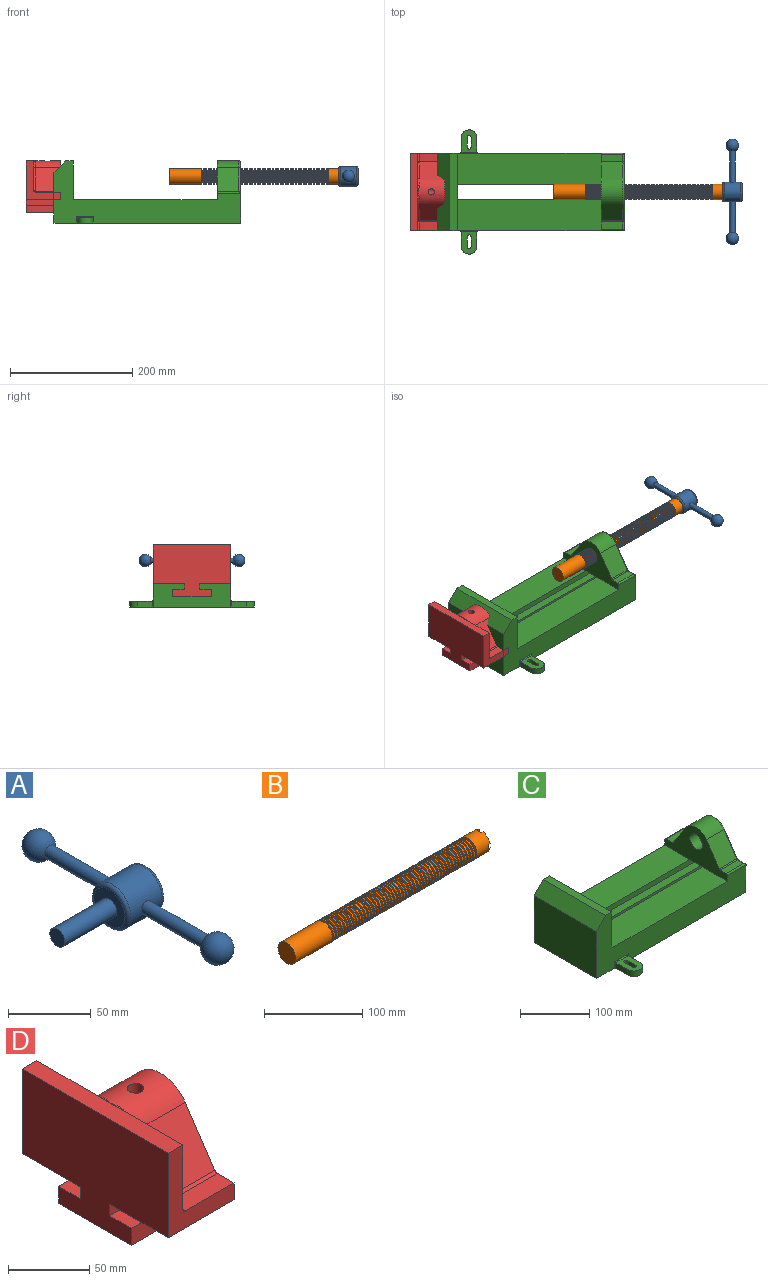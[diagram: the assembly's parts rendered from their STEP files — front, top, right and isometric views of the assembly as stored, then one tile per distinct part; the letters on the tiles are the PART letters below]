
ASSEMBLY  parts=4 mates=4
PART A: 11 faces, bbox 76.2x172.7x34.4 mm
  f0: sphere r=10.16mm, area 1231.8mm2, adj f1
  f1: cylinder r=4.45mm len=51.82mm, axis (0,1,0), area 1438.5mm2, adj f0,f4
  f2: sphere r=10.16mm, area 1231.8mm2, adj f3
  f3: cylinder r=4.45mm len=51.82mm, axis (0,1,0), area 1438.5mm2, adj f2,f4
  f4: cylinder r=15.88mm len=31.75mm, axis (-1,0,0), area 2534.7mm2, adj f1,f3,f9,f10
  f5: cylinder r=6.35mm len=44.45mm, axis (-1,0,0), area 1773.5mm2, adj f6,f8
  f6: plane 12.7x12.7mm, normal (-1,0,0), area 126.7mm2, adj f5
  f7: plane 26.67x26.67mm, normal (1,0,0), area 558.6mm2, adj f10
  f8: plane 26.67x26.67mm, normal (-1,0,0), area 432mm2, adj f5,f9
  f9: torus R=13.33mm, axis (1,0,0), area 374.8mm2, adj f4,f8
  f10: torus R=13.33mm, axis (1,0,0), area 374.8mm2, adj f4,f7
PART B: 220 faces, bbox 279.4x25.4x25.4 mm
  f0: cylinder r=12.7mm len=25.4mm, axis (-1,0,0), area 1468.2mm2, adj f1,f2,f3,f5,f7,f208,f209,f210
  f1: plane 9.9x9.9mm, normal (1,0,0), area 62.3mm2, adj f0,f4,f213,f216
  f2: plane 9.9x9.9mm, normal (1,0,0), area 62.3mm2, adj f0,f4,f210,f218
  f3: plane 9.9x9.9mm, normal (1,0,0), area 62.3mm2, adj f0,f4,f209,f212
  f4: cylinder r=6.35mm len=25.4mm, axis (1,0,0), area 960.3mm2, adj f1,f2,f3,f5,f6,f208,f209,f210
  f5: plane 9.9x9.9mm, normal (1,0,0), area 62.3mm2, adj f0,f4,f215,f217
  f6: plane 12.7x12.7mm, normal (1,0,0), area 126.7mm2, adj f4
  f7: cone r=12.7mm half-angle=76deg, axis (1,0,0), area 188mm2, adj f0,f9
  f8: cone r=10.16mm half-angle=76deg, axis (-1,0,0), area 188mm2, adj f9,f10
  f9: cylinder r=10.16mm len=20.32mm, axis (1,0,0), area 81.1mm2, adj f7,f8
  f10: cylinder r=12.7mm len=25.4mm, axis (-1,0,0), area 131.7mm2, adj f8,f11
  f11: cone r=12.7mm half-angle=76deg, axis (1,0,0), area 188mm2, adj f10,f13
  f12: cone r=10.16mm half-angle=76deg, axis (-1,0,0), area 188mm2, adj f13,f14
  f13: cylinder r=10.16mm len=20.32mm, axis (1,0,0), area 81.1mm2, adj f11,f12
  f14: cylinder r=12.7mm len=25.4mm, axis (-1,0,0), area 131.7mm2, adj f12,f15
  f15: cone r=12.7mm half-angle=76deg, axis (1,0,0), area 188mm2, adj f14,f17
  f16: cone r=10.16mm half-angle=76deg, axis (-1,0,0), area 188mm2, adj f17,f18
  f17: cylinder r=10.16mm len=20.32mm, axis (1,0,0), area 81.1mm2, adj f15,f16
  f18: cylinder r=12.7mm len=25.4mm, axis (-1,0,0), area 131.7mm2, adj f16,f19
  f19: cone r=12.7mm half-angle=76deg, axis (1,0,0), area 188mm2, adj f18,f21
  f20: cone r=10.16mm half-angle=76deg, axis (-1,0,0), area 188mm2, adj f21,f22
  f21: cylinder r=10.16mm len=20.32mm, axis (1,0,0), area 81.1mm2, adj f19,f20
  f22: cylinder r=12.7mm len=25.4mm, axis (-1,0,0), area 131.7mm2, adj f20,f23
  f23: cone r=12.7mm half-angle=76deg, axis (1,0,0), area 188mm2, adj f22,f25
  f24: cone r=10.16mm half-angle=76deg, axis (-1,0,0), area 188mm2, adj f25,f26
  f25: cylinder r=10.16mm len=20.32mm, axis (1,0,0), area 81.1mm2, adj f23,f24
  f26: cylinder r=12.7mm len=25.4mm, axis (-1,0,0), area 131.7mm2, adj f24,f27
  f27: cone r=12.7mm half-angle=76deg, axis (1,0,0), area 188mm2, adj f26,f29
  f28: cone r=10.16mm half-angle=76deg, axis (-1,0,0), area 188mm2, adj f29,f30
  f29: cylinder r=10.16mm len=20.32mm, axis (1,0,0), area 81.1mm2, adj f27,f28
  f30: cylinder r=12.7mm len=25.4mm, axis (-1,0,0), area 131.7mm2, adj f28,f31
  f31: cone r=12.7mm half-angle=76deg, axis (1,0,0), area 188mm2, adj f30,f33
  f32: cone r=10.16mm half-angle=76deg, axis (-1,0,0), area 188mm2, adj f33,f34
  f33: cylinder r=10.16mm len=20.32mm, axis (1,0,0), area 81.1mm2, adj f31,f32
  f34: cylinder r=12.7mm len=25.4mm, axis (-1,0,0), area 131.7mm2, adj f32,f35
  f35: cone r=12.7mm half-angle=76deg, axis (1,0,0), area 188mm2, adj f34,f37
  f36: cone r=10.16mm half-angle=76deg, axis (-1,0,0), area 188mm2, adj f37,f38
  f37: cylinder r=10.16mm len=20.32mm, axis (1,0,0), area 81.1mm2, adj f35,f36
  f38: cylinder r=12.7mm len=25.4mm, axis (-1,0,0), area 131.7mm2, adj f36,f39
  f39: cone r=12.7mm half-angle=76deg, axis (1,0,0), area 188mm2, adj f38,f41
  f40: cone r=10.16mm half-angle=76deg, axis (-1,0,0), area 188mm2, adj f41,f42
  f41: cylinder r=10.16mm len=20.32mm, axis (1,0,0), area 81.1mm2, adj f39,f40
  f42: cylinder r=12.7mm len=25.4mm, axis (-1,0,0), area 131.7mm2, adj f40,f43
  f43: cone r=12.7mm half-angle=76deg, axis (1,0,0), area 188mm2, adj f42,f45
  f44: cone r=10.16mm half-angle=76deg, axis (-1,0,0), area 188mm2, adj f45,f46
  f45: cylinder r=10.16mm len=20.32mm, axis (1,0,0), area 81.1mm2, adj f43,f44
  f46: cylinder r=12.7mm len=25.4mm, axis (-1,0,0), area 131.7mm2, adj f44,f47
  f47: cone r=12.7mm half-angle=76deg, axis (1,0,0), area 188mm2, adj f46,f49
  f48: cone r=10.16mm half-angle=76deg, axis (-1,0,0), area 188mm2, adj f49,f50
  f49: cylinder r=10.16mm len=20.32mm, axis (1,0,0), area 81.1mm2, adj f47,f48
  f50: cylinder r=12.7mm len=25.4mm, axis (-1,0,0), area 131.7mm2, adj f48,f51
  f51: cone r=12.7mm half-angle=76deg, axis (1,0,0), area 188mm2, adj f50,f53
  f52: cone r=10.16mm half-angle=76deg, axis (-1,0,0), area 188mm2, adj f53,f54
  f53: cylinder r=10.16mm len=20.32mm, axis (1,0,0), area 81.1mm2, adj f51,f52
  f54: cylinder r=12.7mm len=25.4mm, axis (-1,0,0), area 131.7mm2, adj f52,f55
  f55: cone r=12.7mm half-angle=76deg, axis (1,0,0), area 188mm2, adj f54,f57
  f56: cone r=10.16mm half-angle=76deg, axis (-1,0,0), area 188mm2, adj f57,f58
  f57: cylinder r=10.16mm len=20.32mm, axis (1,0,0), area 81.1mm2, adj f55,f56
  f58: cylinder r=12.7mm len=25.4mm, axis (-1,0,0), area 131.7mm2, adj f56,f59
  f59: cone r=12.7mm half-angle=76deg, axis (1,0,0), area 188mm2, adj f58,f61
  f60: cone r=10.16mm half-angle=76deg, axis (-1,0,0), area 188mm2, adj f61,f62
  f61: cylinder r=10.16mm len=20.32mm, axis (1,0,0), area 81.1mm2, adj f59,f60
  f62: cylinder r=12.7mm len=25.4mm, axis (-1,0,0), area 131.7mm2, adj f60,f63
  f63: cone r=12.7mm half-angle=76deg, axis (1,0,0), area 188mm2, adj f62,f65
  f64: cone r=10.16mm half-angle=76deg, axis (-1,0,0), area 188mm2, adj f65,f66
  f65: cylinder r=10.16mm len=20.32mm, axis (1,0,0), area 81.1mm2, adj f63,f64
  f66: cylinder r=12.7mm len=25.4mm, axis (-1,0,0), area 131.7mm2, adj f64,f67
  f67: cone r=12.7mm half-angle=76deg, axis (1,0,0), area 188mm2, adj f66,f69
  f68: cone r=10.16mm half-angle=76deg, axis (-1,0,0), area 188mm2, adj f69,f70
  f69: cylinder r=10.16mm len=20.32mm, axis (1,0,0), area 81.1mm2, adj f67,f68
  f70: cylinder r=12.7mm len=25.4mm, axis (-1,0,0), area 131.7mm2, adj f68,f71
  f71: cone r=12.7mm half-angle=76deg, axis (1,0,0), area 188mm2, adj f70,f73
  f72: cone r=10.16mm half-angle=76deg, axis (-1,0,0), area 188mm2, adj f73,f74
  f73: cylinder r=10.16mm len=20.32mm, axis (1,0,0), area 81.1mm2, adj f71,f72
  f74: cylinder r=12.7mm len=25.4mm, axis (-1,0,0), area 131.7mm2, adj f72,f75
  f75: cone r=12.7mm half-angle=76deg, axis (1,0,0), area 188mm2, adj f74,f77
  f76: cone r=10.16mm half-angle=76deg, axis (-1,0,0), area 188mm2, adj f77,f78
  f77: cylinder r=10.16mm len=20.32mm, axis (1,0,0), area 81.1mm2, adj f75,f76
  f78: cylinder r=12.7mm len=25.4mm, axis (-1,0,0), area 131.7mm2, adj f76,f79
  f79: cone r=12.7mm half-angle=76deg, axis (1,0,0), area 188mm2, adj f78,f81
  f80: cone r=10.16mm half-angle=76deg, axis (-1,0,0), area 188mm2, adj f81,f82
  f81: cylinder r=10.16mm len=20.32mm, axis (1,0,0), area 81.1mm2, adj f79,f80
  f82: cylinder r=12.7mm len=25.4mm, axis (-1,0,0), area 131.7mm2, adj f80,f83
  f83: cone r=12.7mm half-angle=76deg, axis (1,0,0), area 188mm2, adj f82,f85
  f84: cone r=10.16mm half-angle=76deg, axis (-1,0,0), area 188mm2, adj f85,f86
  f85: cylinder r=10.16mm len=20.32mm, axis (1,0,0), area 81.1mm2, adj f83,f84
  f86: cylinder r=12.7mm len=25.4mm, axis (-1,0,0), area 131.7mm2, adj f84,f87
  f87: cone r=12.7mm half-angle=76deg, axis (1,0,0), area 188mm2, adj f86,f89
  f88: cone r=10.16mm half-angle=76deg, axis (-1,0,0), area 188mm2, adj f89,f90
  f89: cylinder r=10.16mm len=20.32mm, axis (1,0,0), area 81.1mm2, adj f87,f88
  f90: cylinder r=12.7mm len=25.4mm, axis (-1,0,0), area 131.7mm2, adj f88,f91
  f91: cone r=12.7mm half-angle=76deg, axis (1,0,0), area 188mm2, adj f90,f93
  f92: cone r=10.16mm half-angle=76deg, axis (-1,0,0), area 188mm2, adj f93,f94
  f93: cylinder r=10.16mm len=20.32mm, axis (1,0,0), area 81.1mm2, adj f91,f92
  f94: cylinder r=12.7mm len=25.4mm, axis (-1,0,0), area 131.7mm2, adj f92,f95
  f95: cone r=12.7mm half-angle=76deg, axis (1,0,0), area 188mm2, adj f94,f97
  f96: cone r=10.16mm half-angle=76deg, axis (-1,0,0), area 188mm2, adj f97,f98
  f97: cylinder r=10.16mm len=20.32mm, axis (1,0,0), area 81.1mm2, adj f95,f96
  f98: cylinder r=12.7mm len=25.4mm, axis (-1,0,0), area 131.7mm2, adj f96,f99
  f99: cone r=12.7mm half-angle=76deg, axis (1,0,0), area 188mm2, adj f98,f101
  f100: cone r=10.16mm half-angle=76deg, axis (-1,0,0), area 188mm2, adj f101,f102
  f101: cylinder r=10.16mm len=20.32mm, axis (1,0,0), area 81.1mm2, adj f99,f100
  f102: cylinder r=12.7mm len=25.4mm, axis (-1,0,0), area 131.7mm2, adj f100,f103
  f103: cone r=12.7mm half-angle=76deg, axis (1,0,0), area 188mm2, adj f102,f105
  f104: cone r=10.16mm half-angle=76deg, axis (-1,0,0), area 188mm2, adj f105,f106
  f105: cylinder r=10.16mm len=20.32mm, axis (1,0,0), area 81.1mm2, adj f103,f104
  f106: cylinder r=12.7mm len=25.4mm, axis (-1,0,0), area 131.7mm2, adj f104,f107
  f107: cone r=12.7mm half-angle=76deg, axis (1,0,0), area 188mm2, adj f106,f109
  f108: cone r=10.16mm half-angle=76deg, axis (-1,0,0), area 188mm2, adj f109,f110
  f109: cylinder r=10.16mm len=20.32mm, axis (1,0,0), area 81.1mm2, adj f107,f108
  f110: cylinder r=12.7mm len=25.4mm, axis (-1,0,0), area 131.7mm2, adj f108,f111
  f111: cone r=12.7mm half-angle=76deg, axis (1,0,0), area 188mm2, adj f110,f113
  f112: cone r=10.16mm half-angle=76deg, axis (-1,0,0), area 188mm2, adj f113,f114
  f113: cylinder r=10.16mm len=20.32mm, axis (1,0,0), area 81.1mm2, adj f111,f112
  f114: cylinder r=12.7mm len=25.4mm, axis (-1,0,0), area 131.7mm2, adj f112,f115
  f115: cone r=12.7mm half-angle=76deg, axis (1,0,0), area 188mm2, adj f114,f117
  f116: cone r=10.16mm half-angle=76deg, axis (-1,0,0), area 188mm2, adj f117,f118
  f117: cylinder r=10.16mm len=20.32mm, axis (1,0,0), area 81.1mm2, adj f115,f116
  f118: cylinder r=12.7mm len=25.4mm, axis (-1,0,0), area 131.7mm2, adj f116,f119
  f119: cone r=12.7mm half-angle=76deg, axis (1,0,0), area 188mm2, adj f118,f121
  f120: cone r=10.16mm half-angle=76deg, axis (-1,0,0), area 188mm2, adj f121,f122
  f121: cylinder r=10.16mm len=20.32mm, axis (1,0,0), area 81.1mm2, adj f119,f120
  f122: cylinder r=12.7mm len=25.4mm, axis (-1,0,0), area 131.7mm2, adj f120,f123
  f123: cone r=12.7mm half-angle=76deg, axis (1,0,0), area 188mm2, adj f122,f125
  f124: cone r=10.16mm half-angle=76deg, axis (-1,0,0), area 188mm2, adj f125,f126
  f125: cylinder r=10.16mm len=20.32mm, axis (1,0,0), area 81.1mm2, adj f123,f124
  f126: cylinder r=12.7mm len=25.4mm, axis (-1,0,0), area 131.7mm2, adj f124,f127
  f127: cone r=12.7mm half-angle=76deg, axis (1,0,0), area 188mm2, adj f126,f129
  f128: cone r=10.16mm half-angle=76deg, axis (-1,0,0), area 188mm2, adj f129,f130
  f129: cylinder r=10.16mm len=20.32mm, axis (1,0,0), area 81.1mm2, adj f127,f128
  f130: cylinder r=12.7mm len=25.4mm, axis (-1,0,0), area 131.7mm2, adj f128,f131
  f131: cone r=12.7mm half-angle=76deg, axis (1,0,0), area 188mm2, adj f130,f133
  f132: cone r=10.16mm half-angle=76deg, axis (-1,0,0), area 188mm2, adj f133,f134
  f133: cylinder r=10.16mm len=20.32mm, axis (1,0,0), area 81.1mm2, adj f131,f132
  f134: cylinder r=12.7mm len=25.4mm, axis (-1,0,0), area 131.7mm2, adj f132,f135
  f135: cone r=12.7mm half-angle=76deg, axis (1,0,0), area 188mm2, adj f134,f137
  f136: cone r=10.16mm half-angle=76deg, axis (-1,0,0), area 188mm2, adj f137,f138
  f137: cylinder r=10.16mm len=20.32mm, axis (1,0,0), area 81.1mm2, adj f135,f136
  f138: cylinder r=12.7mm len=25.4mm, axis (-1,0,0), area 131.7mm2, adj f136,f139
  f139: cone r=12.7mm half-angle=76deg, axis (1,0,0), area 188mm2, adj f138,f141
  f140: cone r=10.16mm half-angle=76deg, axis (-1,0,0), area 188mm2, adj f141,f142
  f141: cylinder r=10.16mm len=20.32mm, axis (1,0,0), area 81.1mm2, adj f139,f140
  f142: cylinder r=12.7mm len=25.4mm, axis (-1,0,0), area 131.7mm2, adj f140,f143
  f143: cone r=12.7mm half-angle=76deg, axis (1,0,0), area 188mm2, adj f142,f145
  f144: cone r=10.16mm half-angle=76deg, axis (-1,0,0), area 188mm2, adj f145,f146
  f145: cylinder r=10.16mm len=20.32mm, axis (1,0,0), area 81.1mm2, adj f143,f144
  f146: cylinder r=12.7mm len=25.4mm, axis (-1,0,0), area 131.7mm2, adj f144,f147
  f147: cone r=12.7mm half-angle=76deg, axis (1,0,0), area 188mm2, adj f146,f149
  f148: cone r=10.16mm half-angle=76deg, axis (-1,0,0), area 188mm2, adj f149,f150
  f149: cylinder r=10.16mm len=20.32mm, axis (1,0,0), area 81.1mm2, adj f147,f148
  f150: cylinder r=12.7mm len=25.4mm, axis (-1,0,0), area 131.7mm2, adj f148,f151
  f151: cone r=12.7mm half-angle=76deg, axis (1,0,0), area 188mm2, adj f150,f153
  f152: cone r=10.16mm half-angle=76deg, axis (-1,0,0), area 188mm2, adj f153,f154
  f153: cylinder r=10.16mm len=20.32mm, axis (1,0,0), area 81.1mm2, adj f151,f152
  f154: cylinder r=12.7mm len=25.4mm, axis (-1,0,0), area 131.7mm2, adj f152,f155
  f155: cone r=12.7mm half-angle=76deg, axis (1,0,0), area 188mm2, adj f154,f157
  f156: cone r=10.16mm half-angle=76deg, axis (-1,0,0), area 188mm2, adj f157,f158
  f157: cylinder r=10.16mm len=20.32mm, axis (1,0,0), area 81.1mm2, adj f155,f156
  f158: cylinder r=12.7mm len=25.4mm, axis (-1,0,0), area 131.7mm2, adj f156,f159
  f159: cone r=12.7mm half-angle=76deg, axis (1,0,0), area 188mm2, adj f158,f161
  f160: cone r=10.16mm half-angle=76deg, axis (-1,0,0), area 188mm2, adj f161,f162
  f161: cylinder r=10.16mm len=20.32mm, axis (1,0,0), area 81.1mm2, adj f159,f160
  f162: cylinder r=12.7mm len=25.4mm, axis (-1,0,0), area 131.7mm2, adj f160,f163
  f163: cone r=12.7mm half-angle=76deg, axis (1,0,0), area 188mm2, adj f162,f165
  f164: cone r=10.16mm half-angle=76deg, axis (-1,0,0), area 188mm2, adj f165,f166
  f165: cylinder r=10.16mm len=20.32mm, axis (1,0,0), area 81.1mm2, adj f163,f164
  f166: cylinder r=12.7mm len=25.4mm, axis (-1,0,0), area 131.7mm2, adj f164,f167
  f167: cone r=12.7mm half-angle=76deg, axis (1,0,0), area 188mm2, adj f166,f169
  f168: cone r=10.16mm half-angle=76deg, axis (-1,0,0), area 188mm2, adj f169,f170
  f169: cylinder r=10.16mm len=20.32mm, axis (1,0,0), area 81.1mm2, adj f167,f168
  f170: cylinder r=12.7mm len=25.4mm, axis (-1,0,0), area 131.7mm2, adj f168,f171
  f171: cone r=12.7mm half-angle=76deg, axis (1,0,0), area 188mm2, adj f170,f173
  f172: cone r=10.16mm half-angle=76deg, axis (-1,0,0), area 188mm2, adj f173,f174
  f173: cylinder r=10.16mm len=20.32mm, axis (1,0,0), area 81.1mm2, adj f171,f172
  f174: cylinder r=12.7mm len=25.4mm, axis (-1,0,0), area 131.7mm2, adj f172,f175
  f175: cone r=12.7mm half-angle=76deg, axis (1,0,0), area 188mm2, adj f174,f177
  f176: cone r=10.16mm half-angle=76deg, axis (-1,0,0), area 188mm2, adj f177,f178
  f177: cylinder r=10.16mm len=20.32mm, axis (1,0,0), area 81.1mm2, adj f175,f176
  f178: cylinder r=12.7mm len=25.4mm, axis (-1,0,0), area 131.7mm2, adj f176,f179
  f179: cone r=12.7mm half-angle=76deg, axis (1,0,0), area 188mm2, adj f178,f181
  f180: cone r=10.16mm half-angle=76deg, axis (-1,0,0), area 188mm2, adj f181,f182
  f181: cylinder r=10.16mm len=20.32mm, axis (1,0,0), area 81.1mm2, adj f179,f180
  f182: cylinder r=12.7mm len=25.4mm, axis (-1,0,0), area 131.7mm2, adj f180,f183
  f183: cone r=12.7mm half-angle=76deg, axis (1,0,0), area 188mm2, adj f182,f185
  f184: cone r=10.16mm half-angle=76deg, axis (-1,0,0), area 188mm2, adj f185,f186
  f185: cylinder r=10.16mm len=20.32mm, axis (1,0,0), area 81.1mm2, adj f183,f184
  f186: cylinder r=12.7mm len=25.4mm, axis (-1,0,0), area 131.7mm2, adj f184,f187
  f187: cone r=12.7mm half-angle=76deg, axis (1,0,0), area 188mm2, adj f186,f189
  f188: cone r=10.16mm half-angle=76deg, axis (-1,0,0), area 188mm2, adj f189,f190
  f189: cylinder r=10.16mm len=20.32mm, axis (1,0,0), area 81.1mm2, adj f187,f188
  f190: cylinder r=12.7mm len=25.4mm, axis (-1,0,0), area 131.7mm2, adj f188,f191
  f191: cone r=12.7mm half-angle=76deg, axis (1,0,0), area 188mm2, adj f190,f193
  f192: cone r=10.16mm half-angle=76deg, axis (-1,0,0), area 188mm2, adj f193,f194
  f193: cylinder r=10.16mm len=20.32mm, axis (1,0,0), area 81.1mm2, adj f191,f192
  f194: cylinder r=12.7mm len=25.4mm, axis (-1,0,0), area 131.7mm2, adj f192,f195
  f195: cone r=12.7mm half-angle=76deg, axis (1,0,0), area 188mm2, adj f194,f197
  f196: cone r=10.16mm half-angle=76deg, axis (-1,0,0), area 188mm2, adj f197,f198
  f197: cylinder r=10.16mm len=20.32mm, axis (1,0,0), area 81.1mm2, adj f195,f196
  f198: cylinder r=12.7mm len=25.4mm, axis (-1,0,0), area 131.7mm2, adj f196,f199
  f199: cone r=12.7mm half-angle=76deg, axis (1,0,0), area 188mm2, adj f198,f201
  f200: cone r=10.16mm half-angle=76deg, axis (-1,0,0), area 188mm2, adj f201,f202
  f201: cylinder r=10.16mm len=20.32mm, axis (1,0,0), area 81.1mm2, adj f199,f200
  f202: cylinder r=12.7mm len=25.4mm, axis (-1,0,0), area 131.7mm2, adj f200,f203
  f203: cone r=12.7mm half-angle=76deg, axis (1,0,0), area 188mm2, adj f202,f205
  f204: cone r=10.16mm half-angle=76deg, axis (-1,0,0), area 188mm2, adj f205,f207
  f205: cylinder r=10.16mm len=20.32mm, axis (1,0,0), area 81.1mm2, adj f203,f204
  f206: plane 25.4x25.4mm, normal (-1,0,0), area 506.7mm2, adj f207
  f207: cylinder r=12.7mm len=52.45mm, axis (-1,0,0), area 4185.4mm2, adj f204,f206
  f208: plane 6.88x5.08mm, normal (1,0,0), area 32.7mm2, adj f0,f4,f209,f210
  f209: plane 6.62x2.54mm, normal (0,-1,0), area 16.8mm2, adj f0,f3,f4,f208
  f210: plane 6.62x2.54mm, normal (0,1,0), area 16.8mm2, adj f0,f2,f4,f208
  f211: plane 6.88x5.08mm, normal (1,0,0), area 32.7mm2, adj f0,f4,f212,f213
  f212: plane 6.62x2.54mm, normal (0,0,1), area 16.8mm2, adj f0,f3,f4,f211
  f213: plane 6.62x2.54mm, normal (0,0,-1), area 16.8mm2, adj f0,f1,f4,f211
  f214: plane 6.88x5.08mm, normal (1,0,0), area 32.7mm2, adj f0,f4,f215,f216
  f215: plane 6.62x2.54mm, normal (0,1,0), area 16.8mm2, adj f0,f4,f5,f214
  f216: plane 6.62x2.54mm, normal (0,-1,0), area 16.8mm2, adj f0,f1,f4,f214
  f217: plane 6.62x2.54mm, normal (0,0,-1), area 16.8mm2, adj f0,f4,f5,f219
  f218: plane 6.62x2.54mm, normal (0,0,1), area 16.8mm2, adj f0,f2,f4,f219
  f219: plane 6.88x5.08mm, normal (1,0,0), area 32.7mm2, adj f0,f4,f217,f218
PART C: 61 faces, bbox 304.8x203.2x103.7 mm
  f0: plane 304.8x101.6mm, normal (0,1,0), area 13520.3mm2, adj f3,f4,f5,f6,f7,f8,f9,f16
  f1: plane 304.8x101.6mm, normal (0,-1,0), area 13520.3mm2, adj f2,f3,f5,f6,f7,f8,f9,f16
  f2: plane 234.95x50.8mm, normal (0,0,1), area 11935.5mm2, adj f1,f5,f16,f26
  f3: plane 127x99.06mm, normal (1,0,0), area 7097.5mm2, adj f0,f1,f9,f14,f17,f18,f19,f20
  f4: plane 234.95x50.8mm, normal (0,0,1), area 11935.5mm2, adj f0,f5,f16,f27
  f5: plane 127x101.6mm, normal (1,0,0), area 9516.1mm2, adj f0,f1,f2,f4,f6,f9,f18,f19
  f6: plane 127x12.7mm, normal (0,0,1), area 1612.9mm2, adj f0,f1,f5,f7
  f7: plane 127x19.05mm, normal (-0.71,0,0.71), area 3421.5mm2, adj f0,f1,f6,f8
  f8: plane 127x82.55mm, normal (-1,0,0), area 10483.8mm2, adj f0,f1,f7,f9
  f9: plane 304.8x203.2mm, normal (0,0,-1), area 33298.3mm2, adj f0,f1,f3,f5,f8,f21,f22,f39
  f10: plane 35.56x11.98mm, normal (0,0,1), area 426mm2, adj f16,f28,f29,f30
  f11: plane 38.43x35.56mm, normal (0,0.83,0.56), area 1645.4mm2, adj f12,f16,f29,f32
  f12: cylinder r=25.4mm len=42.19mm, axis (1,0,0), area 1770.2mm2, adj f11,f13,f16,f33
  f13: plane 38.43x35.56mm, normal (0,-0.83,0.56), area 1645.4mm2, adj f12,f16,f34,f35
  f14: cylinder r=12.7mm len=38.1mm, axis (1,0,0), area 3040.2mm2, adj f3,f16
  f15: plane 35.56x11.98mm, normal (0,0,1), area 426mm2, adj f16,f34,f36,f38
  f16: plane 127x63.5mm, normal (-1,0,0), area 4155.5mm2, adj f0,f1,f2,f4,f10,f11,f12,f13
  f17: plane 38.1x25.4mm, normal (0,0,-1), area 967.7mm2, adj f3,f16,f26,f27
  f18: plane 273.05x19.05mm, normal (0,0,-1), area 5201.6mm2, adj f3,f5,f19,f26
  f19: plane 273.05x12.7mm, normal (0,1,0), area 3467.7mm2, adj f3,f5,f18,f20
  f20: plane 273.05x19.05mm, normal (0,0,1), area 5201.6mm2, adj f3,f5,f19,f21
  f21: plane 273.05x16.51mm, normal (0,1,0), area 4508.1mm2, adj f3,f5,f9,f20
  f22: plane 273.05x16.51mm, normal (0,-1,0), area 4508.1mm2, adj f3,f5,f9,f23
  f23: plane 273.05x19.05mm, normal (0,0,1), area 5201.6mm2, adj f3,f5,f22,f24
  f24: plane 273.05x12.7mm, normal (0,-1,0), area 3467.7mm2, adj f3,f5,f23,f25
  f25: plane 273.05x19.05mm, normal (0,0,-1), area 5201.6mm2, adj f3,f5,f24,f27
  f26: plane 273.05x8.89mm, normal (0,1,0), area 2427.4mm2, adj f2,f3,f5,f17,f18
  f27: plane 273.05x8.89mm, normal (0,-1,0), area 2427.4mm2, adj f3,f4,f5,f17,f25
  f28: cylinder r=2.54mm len=38.1mm, axis (1,0,0), area 148.3mm2, adj f0,f10,f16,f30
  f29: cylinder r=2.54mm len=35.56mm, axis (-1,0,0), area 88.5mm2, adj f10,f11,f16,f31
  f30: cylinder r=2.54mm len=14.52mm, axis (0,1,0), area 54.3mm2, adj f3,f10,f28,f31
  f31: torus R=5.08mm, axis (-1,0,0), area 13.5mm2, adj f3,f29,f30,f32
  f32: cylinder r=2.54mm len=39.84mm, axis (0,0.56,-0.83), area 184.6mm2, adj f3,f11,f31,f33
  f33: torus R=22.86mm, axis (-1,0,0), area 191.4mm2, adj f3,f12,f32,f35
  f34: cylinder r=2.54mm len=35.56mm, axis (-1,0,0), area 88.5mm2, adj f13,f15,f16,f37
  f35: cylinder r=2.54mm len=39.84mm, axis (0,0.56,0.83), area 184.6mm2, adj f3,f13,f33,f37
  f36: cylinder r=2.54mm len=38.1mm, axis (-1,0,0), area 148.3mm2, adj f1,f15,f16,f38
  f37: torus R=5.08mm, axis (-1,0,0), area 13.5mm2, adj f3,f34,f35,f38
  f38: cylinder r=2.54mm len=14.52mm, axis (0,1,0), area 54.3mm2, adj f3,f15,f36,f37
  f39: plane 23.88x9.53mm, normal (-1,0,0), area 227.4mm2, adj f9,f45,f46,f60
  f40: plane 23.88x9.53mm, normal (1,0,0), area 227.4mm2, adj f9,f45,f46,f58
  f41: cylinder r=3.3mm len=9.53mm, axis (0,0,-1), area 98.8mm2, adj f9,f42,f44,f46
  f42: plane 15.62x9.53mm, normal (-1,0,0), area 148.8mm2, adj f9,f41,f43,f46
  f43: cylinder r=3.3mm len=9.53mm, axis (0,0,-1), area 98.8mm2, adj f9,f42,f44,f46
  f44: plane 15.62x9.53mm, normal (1,0,0), area 148.8mm2, adj f9,f41,f43,f46
  f45: cylinder r=12.7mm len=25.4mm, axis (0,0,-1), area 380mm2, adj f9,f39,f40,f46
  f46: plane 36.58x25.4mm, normal (0,0,1), area 722.4mm2, adj f39,f40,f41,f42,f43,f44,f45,f59
  f47: plane 23.88x9.53mm, normal (-1,0,0), area 227.4mm2, adj f9,f53,f54,f56
  f48: plane 23.88x9.53mm, normal (1,0,0), area 227.4mm2, adj f9,f53,f54,f55
  f49: cylinder r=3.3mm len=9.53mm, axis (0,0,-1), area 98.8mm2, adj f9,f50,f52,f54
  f50: plane 15.62x9.53mm, normal (-1,0,0), area 148.8mm2, adj f9,f49,f51,f54
  f51: cylinder r=3.3mm len=9.53mm, axis (0,0,-1), area 98.8mm2, adj f9,f50,f52,f54
  f52: plane 15.62x9.53mm, normal (1,0,0), area 148.8mm2, adj f9,f49,f51,f54
  f53: cylinder r=12.7mm len=25.4mm, axis (0,0,-1), area 380mm2, adj f9,f47,f48,f54
  f54: plane 36.58x25.4mm, normal (0,0,1), area 722.4mm2, adj f47,f48,f49,f50,f51,f52,f53,f57
  f55: cylinder r=1.52mm len=11.05mm, axis (0,0,-1), area 24.1mm2, adj f0,f9,f48,f57
  f56: cylinder r=1.52mm len=11.05mm, axis (0,0,1), area 24.1mm2, adj f0,f9,f47,f57
  f57: cylinder r=1.52mm len=28.45mm, axis (1,0,0), area 63.5mm2, adj f0,f54,f55,f56
  f58: cylinder r=1.52mm len=11.05mm, axis (0,0,1), area 24.1mm2, adj f1,f9,f40,f59
  f59: cylinder r=1.52mm len=28.45mm, axis (-1,0,0), area 63.5mm2, adj f1,f46,f58,f60
  f60: cylinder r=1.52mm len=11.05mm, axis (0,0,-1), area 24.1mm2, adj f1,f9,f39,f59
PART D: 36 faces, bbox 57.2x127x89 mm
  f0: plane 57.15x50.8mm, normal (0,0,-1), area 2903.2mm2, adj f6,f9,f10,f23
  f1: cylinder r=12.7mm len=44.45mm, axis (1,0,0), area 3464.3mm2, adj f6,f15,f16
  f2: plane 41.91x14.52mm, normal (0,0,1), area 608.5mm2, adj f6,f11,f24,f25
  f3: plane 51.86x48.26mm, normal (1,0,0), area 1495.7mm2, adj f8,f10,f31,f33,f35
  f4: plane 51.86x48.26mm, normal (1,0,0), area 1495.7mm2, adj f8,f11,f24,f28,f29
  f5: plane 57.15x50.8mm, normal (0,0,-1), area 2903.2mm2, adj f6,f9,f11,f22
  f6: plane 127x85.09mm, normal (1,0,0), area 5190.6mm2, adj f0,f1,f2,f5,f7,f10,f11,f12
  f7: plane 41.91x14.52mm, normal (0,0,1), area 608.5mm2, adj f6,f10,f30,f31
  f8: plane 127x12.7mm, normal (0,0,1), area 1612.9mm2, adj f3,f4,f9,f10,f11,f26,f34
  f9: plane 127x85.09mm, normal (-1,0,0), area 9096.8mm2, adj f0,f5,f8,f10,f11,f17,f18,f19
  f10: plane 63.5x57.15mm, normal (0,-1,0), area 1372.3mm2, adj f0,f3,f6,f7,f8,f9,f31
  f11: plane 63.5x57.15mm, normal (0,1,0), area 1372.3mm2, adj f2,f4,f5,f6,f8,f9,f24
  f12: plane 41.91x38.43mm, normal (0,-0.83,0.56), area 1939.2mm2, adj f6,f13,f30,f33
  f13: cylinder r=25.4mm len=44.45mm, axis (1,0,0), area 2026.5mm2, adj f6,f12,f14,f16,f26,f28,f34,f35
  f14: plane 41.91x38.43mm, normal (0,0.83,0.56), area 1939.2mm2, adj f6,f13,f25,f29
  f15: plane 25.4x25.4mm, normal (1,0,0), area 506.7mm2, adj f1
  f16: cylinder r=5.08mm len=13.76mm, axis (0,0,1), area 414mm2, adj f1,f13
  f17: plane 57.15x19.05mm, normal (0,0,1), area 1088.7mm2, adj f6,f9,f18,f23
  f18: plane 57.15x12.7mm, normal (0,-1,0), area 725.8mm2, adj f6,f9,f17,f19
  f19: plane 63.5x57.15mm, normal (0,0,-1), area 3629mm2, adj f6,f9,f18,f20
  f20: plane 57.15x12.7mm, normal (0,1,0), area 725.8mm2, adj f6,f9,f19,f21
  f21: plane 57.15x19.05mm, normal (0,0,1), area 1088.7mm2, adj f6,f9,f20,f22
  f22: plane 57.15x8.89mm, normal (0,1,0), area 508.1mm2, adj f5,f6,f9,f21
  f23: plane 57.15x8.89mm, normal (0,-1,0), area 508.1mm2, adj f0,f6,f9,f17
  f24: cylinder r=2.54mm len=14.52mm, axis (0,-1,0), area 57.9mm2, adj f2,f4,f11,f27
  f25: cylinder r=2.54mm len=41.91mm, axis (1,0,0), area 104.3mm2, adj f2,f6,f14,f27
  f26: bspline ~12.24x2.8mm, area 20.9mm2, adj f8,f13,f28
  f27: sphere r=2.54mm, area 6.3mm2, adj f24,f25,f29
  f28: torus R=27.94mm, axis (1,0,0), area 57.8mm2, adj f4,f13,f26,f29
  f29: cylinder r=2.54mm len=39.84mm, axis (0,-0.56,0.83), area 184.6mm2, adj f4,f14,f27,f28
  f30: cylinder r=2.54mm len=41.91mm, axis (1,0,0), area 104.3mm2, adj f6,f7,f12,f32
  f31: cylinder r=2.54mm len=14.52mm, axis (0,-1,0), area 57.9mm2, adj f3,f7,f10,f32
  f32: sphere r=2.54mm, area 6.3mm2, adj f30,f31,f33
  f33: cylinder r=2.54mm len=39.84mm, axis (0,-0.56,-0.83), area 184.6mm2, adj f3,f12,f32,f35
  f34: bspline ~12.24x2.8mm, area 20.9mm2, adj f8,f13,f35
  f35: torus R=27.94mm, axis (1,0,0), area 57.8mm2, adj f3,f13,f33,f34
PLACE A rot(axis=(-1,0,0),180deg) t=(144.2,-31.52,167.23)mm
PLACE B rot(axis=(-1,0,0),90deg) t=(166.43,-107.72,91.03)mm
PLACE C t=(22.03,-31.52,14.83)mm fixed
PLACE D t=(-55.48,-31.52,14.83)mm
MATE fastened A.f5 <-> B.f4  axis (-1,0,0) through (160.08,-31.52,91.03)mm
MATE slider B.f7 <-> C.f12  axis (1,0,0) through (70.03,-31.52,91.03)mm
MATE slider D.f28 <-> B.f7  axis (1,0,0) through (-271.38,-31.52,91.03)mm
MATE cylindrical B.f7 <-> C.f12  axis (1,0,0) through (2.98,-31.52,91.03)mm
